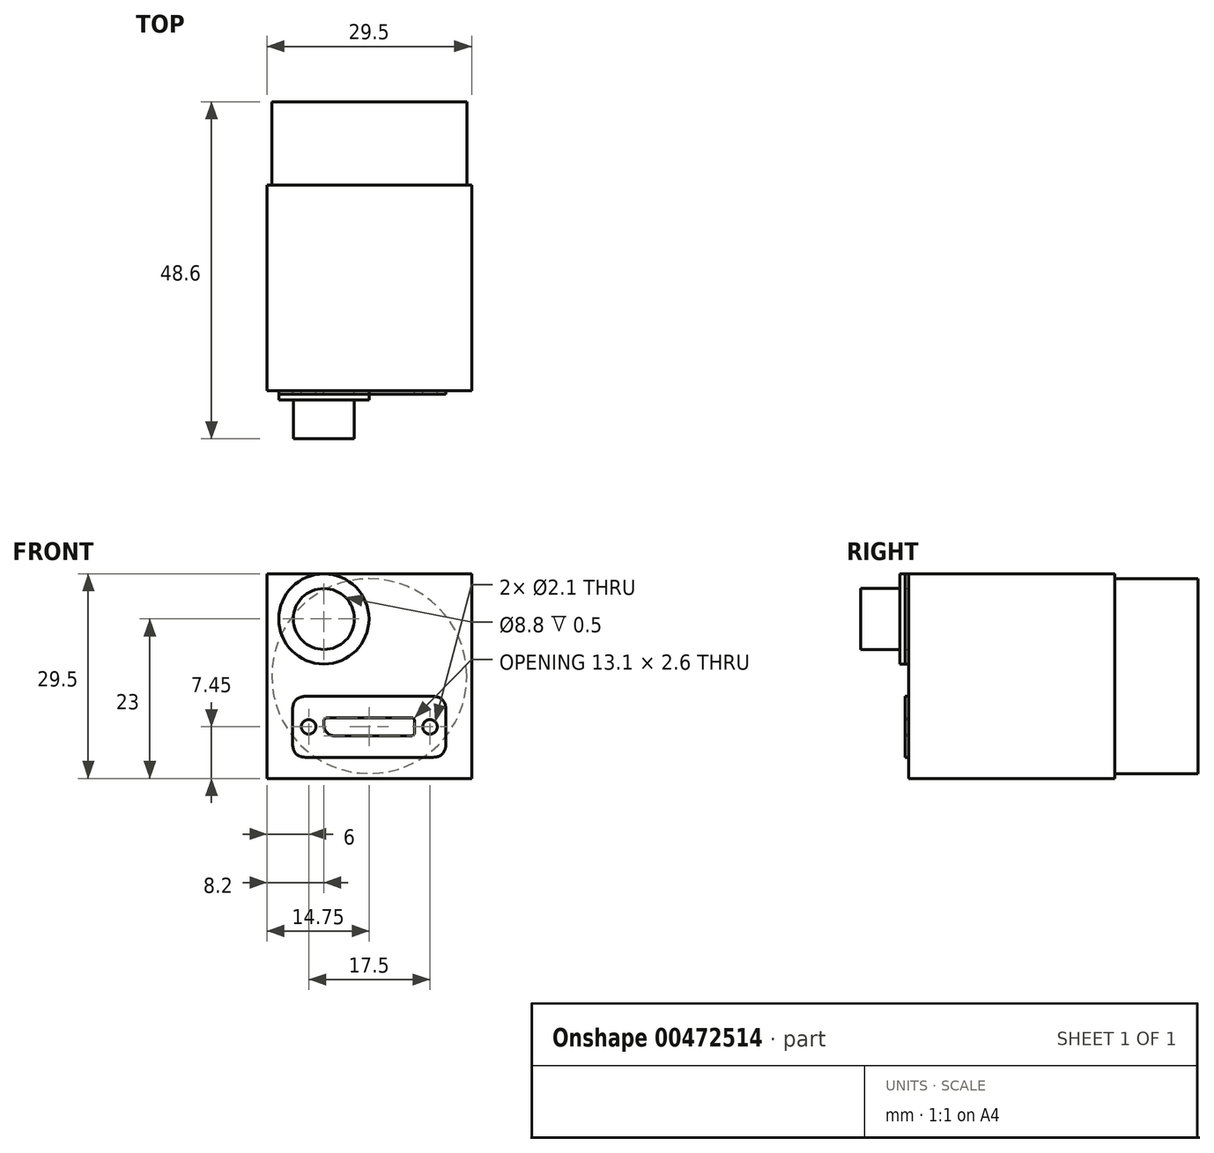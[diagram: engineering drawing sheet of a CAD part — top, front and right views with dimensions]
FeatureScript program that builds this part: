
annotation { "Feature Type Name" : "Feature", "Feature Type Description" : "" }
export const myFeature = defineFeature(function(context is Context, id is Id, definition is map)
    precondition{}
    {
        {
            var Q0;
            Q0=qCreatedBy(makeId("Front.planeOp"),FACE);
            var sketch = newSketch(context, id + "F0", { "sketchPlane" : qUnion([Q0])});
            skCircle(sketch, "E0.cCircle", {"center": v(0, 0) * mm, "radius": 14.75 * mm, "construction": true});
            skLineSegment(sketch, "E0.0", {"start": v(14.75, 14.75) * mm, "end": v(14.75, -14.75) * mm});
            skLineSegment(sketch, "E0.1", {"start": v(14.75, -14.75) * mm, "end": v(-14.75, -14.75) * mm});
            skLineSegment(sketch, "E0.2", {"start": v(-14.75, -14.75) * mm, "end": v(-14.75, 14.75) * mm});
            skLineSegment(sketch, "E0.3", {"start": v(-14.75, 14.75) * mm, "end": v(14.75, 14.75) * mm});
            skPoint(sketch, "E0.0.midPoint", {"position": v(14.75, 0) * mm});
            skCircle(sketch, "E1", {"center": v(0, 0) * mm, "radius": 14.05 * mm});
            skSolve(sketch);
        }
        {
            var Q0;
            Q0=makeQuery(id+"F0.imprint","IMPRINT",FACE,{"disambiguationData":[TD([[makeQuery(id+"F0.imprint","IMPRINT",EDGE,{"derivedFrom":sQuery(id+"F0.wireOp",EDGE,"E1")}),1.0]])]});
            extrude(context, id + "F1", {"entities" : qUnion([Q0]), "oppositeDirection" : true, "depth" : 12 * mm});
        }
        {
            var Q0;
            Q0=makeQuery(id+"F0.imprint","IMPRINT",FACE,{"disambiguationData":[TD([[makeQuery(id+"F0.imprint","IMPRINT",EDGE,{"derivedFrom":sQuery(id+"F0.wireOp",EDGE,"E0.0")}),-1.0]])]});
            extrude(context, id + "F2", {"entities" : qUnion([Q0]), "depth" : 29.7 * mm});
        }
        {
            var Q0;
            Q0=makeQuery(id+"F0.imprint","IMPRINT",FACE,{"disambiguationData":[TD([[makeQuery(id+"F0.imprint","IMPRINT",EDGE,{"derivedFrom":sQuery(id+"F0.wireOp",EDGE,"E1")}),1.0]])]});
            extrude(context, id + "F3", {"entities" : qUnion([Q0]), "depth" : 29.7 * mm});
        }
        {
            var Q0;
            Q0=qCreatedBy(makeId("Front.planeOp"),FACE);
            cPlane(context, id + "F4", {"entities" : qUnion([Q0]), "cplaneType" : CPlaneType.OFFSET, "offset" : 29.7 * mm, "width" : 150 * mm, "height" : 150 * mm});
        }
        {
            var Q0;
            Q0=qCreatedBy(id+"F4.planeOp",FACE);
            var sketch = newSketch(context, id + "F5", { "sketchPlane" : qUnion([Q0])});
            skLineSegment(sketch, "E2", {"start": v(0, 0) * mm, "end": v(0, 8.25) * mm, "construction": true});
            skLineSegment(sketch, "E3", {"start": v(0, 8.25) * mm, "end": v(6.65, 8.25) * mm, "construction": true});
            skLineSegment(sketch, "E4", {"start": v(0, 8.25) * mm, "end": v(0, 14.7) * mm, "construction": true});
            skCircle(sketch, "E5", {"center": v(-6.55, 8.25) * mm, "radius": 6.5 * mm});
            skCircle(sketch, "E6", {"center": v(-6.55, 8.25) * mm, "radius": 4.4 * mm});
            skLineSegment(sketch, "E7", {"start": v(0, 0) * mm, "end": v(0, -7.3) * mm, "construction": true});
            skLineSegment(sketch, "E8.bottom", {"start": v(-11.05, -11.7) * mm, "end": v(11.05, -11.7) * mm});
            skLineSegment(sketch, "E8.top", {"start": v(-11.05, -2.9) * mm, "end": v(11.05, -2.9) * mm});
            skLineSegment(sketch, "E8.left", {"start": v(-11.05, -11.7) * mm, "end": v(-11.05, -2.9) * mm});
            skLineSegment(sketch, "E8.right", {"start": v(11.05, -11.7) * mm, "end": v(11.05, -2.9) * mm});
            skPoint(sketch, "E8.middle", {"position": v(0, -7.3) * mm});
            skLineSegment(sketch, "E9", {"start": v(0, -7.3) * mm, "end": v(-8.75, -7.3) * mm, "construction": true});
            skLineSegment(sketch, "E10.MirrorCS", {"start": v(0, -7.3) * mm, "end": v(8.75, -7.3) * mm, "construction": true});
            skLineSegment(sketch, "E11.bottom", {"start": v(6.55, -8.6) * mm, "end": v(-6.55, -8.6) * mm});
            skLineSegment(sketch, "E11.top", {"start": v(6.55, -6) * mm, "end": v(-6.55, -6) * mm});
            skLineSegment(sketch, "E11.left", {"start": v(6.55, -8.6) * mm, "end": v(6.55, -6) * mm});
            skLineSegment(sketch, "E11.right", {"start": v(-6.55, -8.6) * mm, "end": v(-6.55, -6) * mm});
            skLineSegment(sketch, "E12", {"start": v(0, 8.25) * mm, "end": v(-6.65, 8.25) * mm, "construction": true});
            skSolve(sketch);
        }
        {
            var Q0;
            Q0=makeQuery(id+"F5.imprint","IMPRINT",FACE,{"disambiguationData":[TD([[makeQuery(id+"F5.imprint","IMPRINT",EDGE,{"derivedFrom":sQuery(id+"F5.wireOp",EDGE,"E5")}),1.0]])]});
            extrude(context, id + "F6", {"entities" : qUnion([Q0]), "depth" : 1.3 * mm});
        }
        {
            var Q0;
            Q0=makeQuery(id+"F5.imprint","IMPRINT",FACE,{"disambiguationData":[TD([[makeQuery(id+"F5.imprint","IMPRINT",EDGE,{"derivedFrom":sQuery(id+"F5.wireOp",EDGE,"E6")}),1.0]])]});
            extrude(context, id + "F7", {"entities" : qUnion([Q0]), "operationType" : NewBodyOperationType.ADD, "depth" : 6.9 * mm});
        }
        {
            var Q0;
            Q0=qSketchRegion(id+"F5",true);
            extrude(context, id + "F8", {"entities" : qUnion([Q0]), "depth" : .5 * mm});
        }
        {
            var Q0;
            Q0=makeQuery(id+"F8.opExtrude","SWEPT_EDGE",EDGE,{"disambiguationData":[OSD([sQuery(id+"F5.wireOp",EDGE,"E8.top"),sQuery(id+"F5.wireOp",EDGE,"E8.left")])]});
            var Q1;
            Q1=makeQuery(id+"F8.opExtrude","SWEPT_EDGE",EDGE,{"disambiguationData":[OSD([sQuery(id+"F5.wireOp",EDGE,"E8.top"),sQuery(id+"F5.wireOp",EDGE,"E8.right")])]});
            var Q2;
            Q2=makeQuery(id+"F8.opExtrude","SWEPT_EDGE",EDGE,{"disambiguationData":[OSD([sQuery(id+"F5.wireOp",EDGE,"E8.bottom"),sQuery(id+"F5.wireOp",EDGE,"E8.left")])]});
            var Q3;
            Q3=makeQuery(id+"F8.opExtrude","SWEPT_EDGE",EDGE,{"disambiguationData":[OSD([sQuery(id+"F5.wireOp",EDGE,"E8.bottom"),sQuery(id+"F5.wireOp",EDGE,"E8.right")])]});
            fillet(context, id + "F9", {"entities" : qUnion([Q0, Q1, Q2, Q3]), "radius" : 2 * mm, "tangentPropagation" : true, "rho" : 0.5, "crossSection" : FilletCrossSection.CONIC, "allowEdgeOverflow" : false});
        }
        {
            var Q0;
            Q0=sQuery(id+"F5.wireOp",VERTEX,"E9.end");
            var Q1;
            Q1=sQuery(id+"F5.wireOp",VERTEX,"E10.MirrorCS.end");
            var Q2;
            Q2=makeQuery(id+"F8.opExtrude","SWEPT_BODY",BODY,{"disambiguationData":[OSD([sQuery(id+"F5.wireOp",EDGE,"E8.bottom"),sQuery(id+"F5.wireOp",EDGE,"E8.top"),sQuery(id+"F5.wireOp",EDGE,"E8.left"),sQuery(id+"F5.wireOp",EDGE,"E8.right")])]});
            hole(context, id + "F10", {"style" : HoleStyle.SIMPLE, "endStyle" : HoleEndStyle.THROUGH, "oppositeDirection" : true, "holeDiameter" : 2.1 * mm, "locations" : qUnion([Q0, Q1]), "scope" : qUnion([Q2]), "isTappedThrough" : true});
        }
        {
            var Q0;
            Q0=makeQuery(id+"F8.opExtrude","SWEPT_EDGE",EDGE,{"disambiguationData":[OSD([sQuery(id+"F5.wireOp",EDGE,"E11.top"),sQuery(id+"F5.wireOp",EDGE,"E11.right")])]});
            var Q1;
            Q1=makeQuery(id+"F8.opExtrude","SWEPT_EDGE",EDGE,{"disambiguationData":[OSD([sQuery(id+"F5.wireOp",EDGE,"E11.top"),sQuery(id+"F5.wireOp",EDGE,"E11.left")])]});
            var Q2;
            Q2=makeQuery(id+"F8.opExtrude","SWEPT_EDGE",EDGE,{"disambiguationData":[OSD([sQuery(id+"F5.wireOp",EDGE,"E11.bottom"),sQuery(id+"F5.wireOp",EDGE,"E11.left")])]});
            fillet(context, id + "F11", {"entities" : qUnion([Q0, Q1, Q2]), "radius" : .5 * mm, "tangentPropagation" : true, "allowEdgeOverflow" : false});
        }
        {
            var Q0;
            Q0=makeQuery(id+"F8.opExtrude","SWEPT_EDGE",EDGE,{"disambiguationData":[OSD([sQuery(id+"F5.wireOp",EDGE,"E11.bottom"),sQuery(id+"F5.wireOp",EDGE,"E11.right")])]});
            fillet(context, id + "F12", {"entities" : qUnion([Q0]), "radius" : 1.5 * mm, "tangentPropagation" : true, "allowEdgeOverflow" : false});
        }
    });
